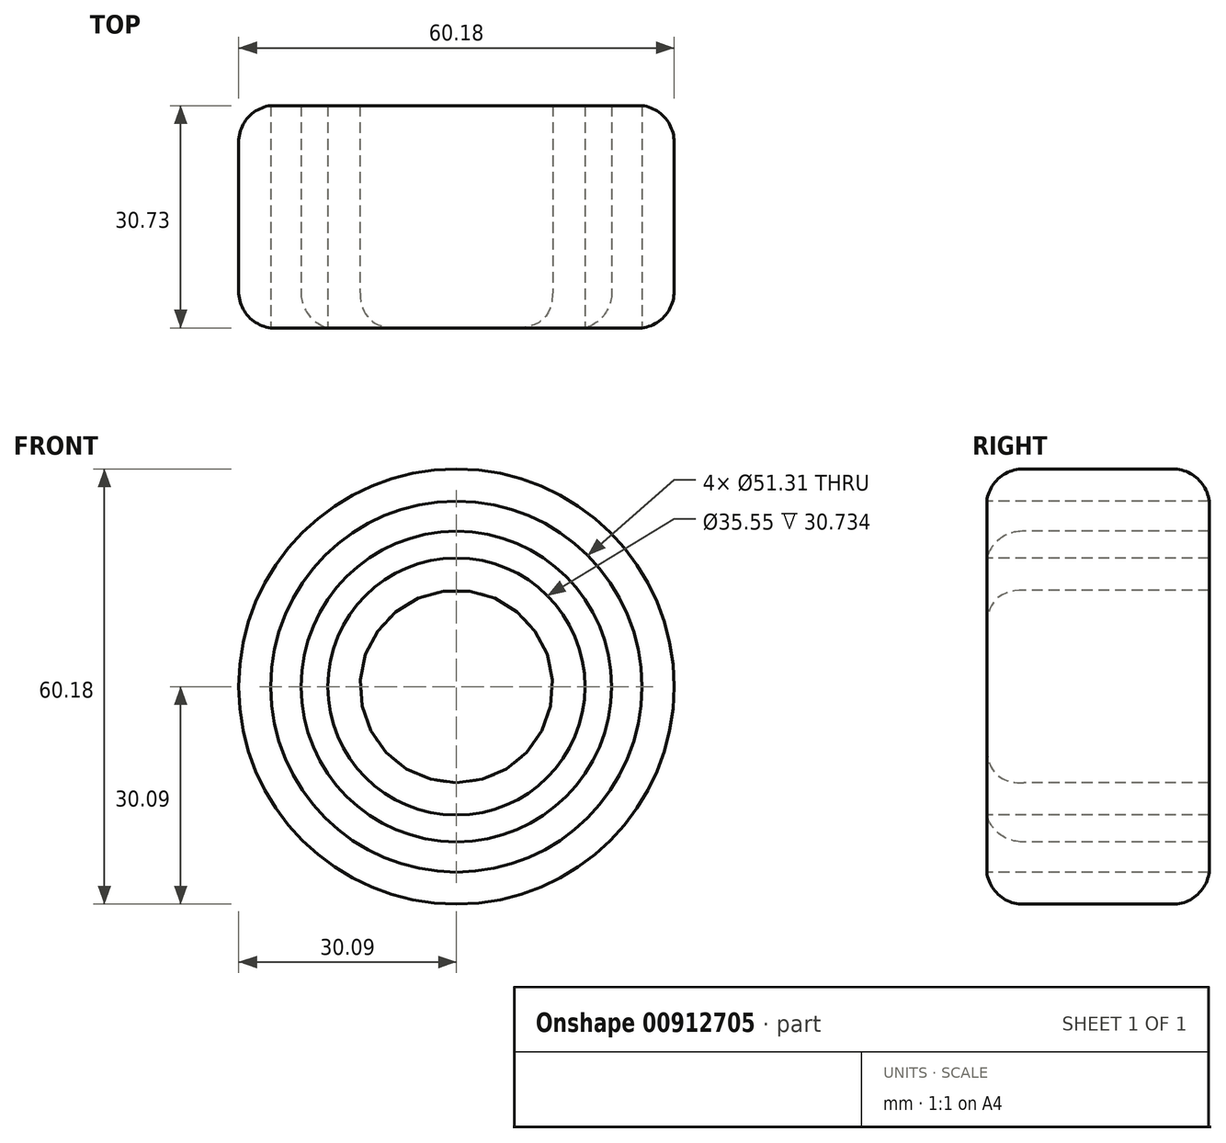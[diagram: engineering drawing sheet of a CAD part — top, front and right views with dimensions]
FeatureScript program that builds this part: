
annotation { "Feature Type Name" : "Feature", "Feature Type Description" : "" }
export const myFeature = defineFeature(function(context is Context, id is Id, definition is map)
    precondition{}
    {
        {
            var Q0;
            Q0=qCreatedBy(makeId("Front.planeOp"),FACE);
            var sketch = newSketch(context, id + "F0", { "sketchPlane" : qUnion([Q0])});
            skCircle(sketch, "E0", {"center": v(0, 0) * mm, "radius": 30.1 * mm});
            skCircle(sketch, "E1", {"center": v(0, 0) * mm, "radius": 25.65 * mm});
            skCircle(sketch, "E2", {"center": v(0, 0) * mm, "radius": 21.47 * mm});
            skCircle(sketch, "E3", {"center": v(0, 0) * mm, "radius": 17.78 * mm});
            skCircle(sketch, "E4", {"center": v(0, 0) * mm, "radius": 13.32 * mm});
            skSolve(sketch);
        }
        {
            var Q0;
            Q0=makeQuery(id+"F0.imprint","IMPRINT",FACE,{"disambiguationData":[TD([[makeQuery(id+"F0.imprint","IMPRINT",EDGE,{"derivedFrom":sQuery(id+"F0.wireOp",EDGE,"E0")}),1.0]])]});
            var Q1;
            Q1=makeQuery(id+"F0.imprint","IMPRINT",FACE,{"disambiguationData":[TD([[makeQuery(id+"F0.imprint","IMPRINT",EDGE,{"derivedFrom":sQuery(id+"F0.wireOp",EDGE,"E2")}),1.0]])]});
            var Q2;
            Q2=makeQuery(id+"F0.imprint","IMPRINT",FACE,{"disambiguationData":[TD([[makeQuery(id+"F0.imprint","IMPRINT",EDGE,{"derivedFrom":sQuery(id+"F0.wireOp",EDGE,"E4")}),1.0]])]});
            extrude(context, id + "F1", {"entities" : qUnion([Q0, Q1, Q2]), "oppositeDirection" : true, "depth" : 5.33 * mm, "offsetDistance" : 25.4 * mm, "hasSecondDirection" : true, "secondDirectionOppositeDirection" : false, "secondDirectionDepth" : 25.4 * mm});
        }
        {
            var Q0;
            Q0=makeQuery(id+"F1.opExtrude","CAP_EDGE",EDGE,{"disambiguationData":[OSD([sQuery(id+"F0.wireOp",EDGE,"E0")])],"isStart":true});
            var Q1;
            Q1=makeQuery(id+"F1.opExtrude","CAP_EDGE",EDGE,{"disambiguationData":[OSD([sQuery(id+"F0.wireOp",EDGE,"E0")])],"isStart":false});
            fillet(context, id + "F2", {"entities" : qUnion([Q0, Q1]), "radius" : 5.08 * mm, "tangentPropagation" : true, "allowEdgeOverflow" : false});
        }
        {
            var Q0;
            Q0=makeQuery(id+"F1.opExtrude","CAP_EDGE",EDGE,{"disambiguationData":[OSD([sQuery(id+"F0.wireOp",EDGE,"E2")])],"isStart":true});
            fillet(context, id + "F3", {"entities" : qUnion([Q0]), "radius" : 5.08 * mm, "tangentPropagation" : true, "allowEdgeOverflow" : false});
        }
        {
            var Q0;
            Q0=makeQuery(id+"F1.opExtrude","CAP_EDGE",EDGE,{"disambiguationData":[OSD([sQuery(id+"F0.wireOp",EDGE,"E4")])],"isStart":true});
            fillet(context, id + "F4", {"entities" : qUnion([Q0]), "radius" : 5.08 * mm, "tangentPropagation" : true, "rho" : 0.5, "crossSection" : FilletCrossSection.CONIC, "allowEdgeOverflow" : false});
        }
        {
            var Q0;
            Q0=makeQuery(id+"F1.opExtrude","SWEPT_BODY",BODY,{"disambiguationData":[OSD([sQuery(id+"F0.wireOp",EDGE,"E0"),sQuery(id+"F0.wireOp",EDGE,"E1")])]});
            var Q1;
            Q1=makeQuery(id+"F3.opFillet","BLEND_FACE",FACE,{"disambiguationData":[OSD([sQuery(id+"F0.wireOp",EDGE,"E2")])]});
            circularPattern(context, id + "F5", {"entities" : qUnion([Q0]), "axis" : qUnion([Q1]), "angle" : 360 * degree, "instanceCount" : 4, "equalSpace" : true});
        }
    });
